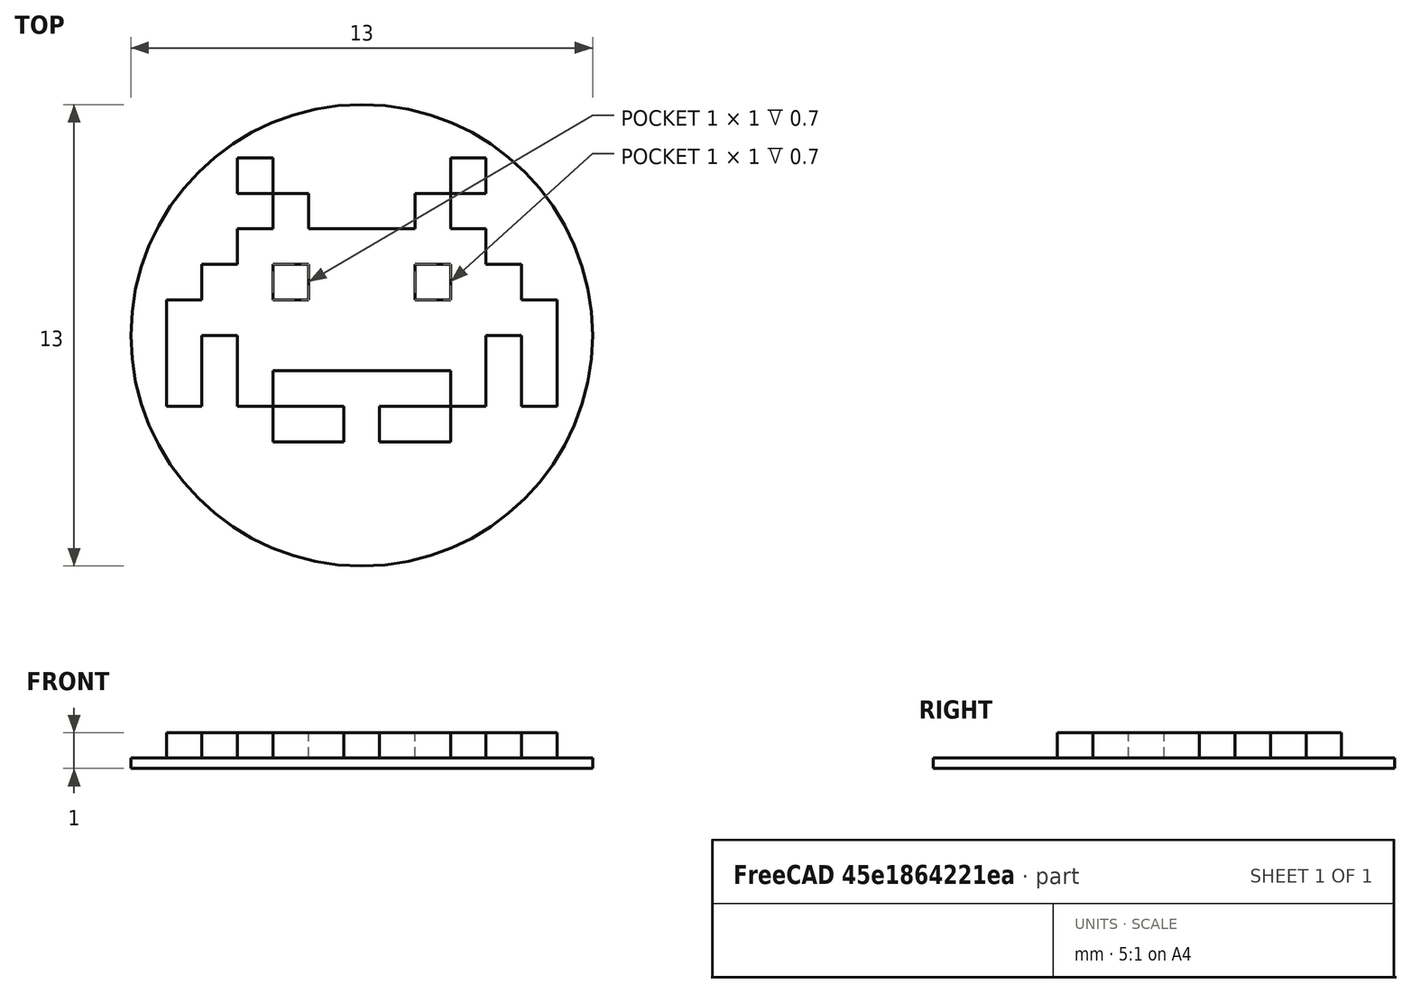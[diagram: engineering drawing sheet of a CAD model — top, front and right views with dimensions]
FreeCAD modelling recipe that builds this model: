
FCSTD DOCUMENT  (FreeCAD 0.20R29177 +233 (Git))
Label: pieza-marcianito
License: Creative Commons Attribution-ShareAlike
LicenseURL: http://creativecommons.org/licenses/by-sa/4.0/
objects: Part::Box×15, Part::MultiFuse×2, Part::Cylinder×1
note: 18 computed .brp shape members not serialized (recipe doc carries the construction recipe); baked Part::Feature solids carry a one-line shape summary decoded from their .brp

FEATURE [Part::Box] Box  label="Cubo"
  AttacherType = Attacher::AttachEngine3D
  Height = 1
  Length = 1
  Width = 1
FEATURE [Part::Box] Box001  label="Cubo001"
  AttacherType = Attacher::AttachEngine3D
  Height = 1
  Length = 1
  Placement = pos=(1,-2,0) rot=(0,0,1;0rad)
  Width = 2
FEATURE [Part::Box] Box002  label="Cubo002"
  AttacherType = Attacher::AttachEngine3D
  Height = 1
  Length = 3
  Placement = pos=(2,-5,0) rot=(0,0,1;0rad)
  Width = 4
FEATURE [Part::Box] Box003  label="Cubo003"
  AttacherType = Attacher::AttachEngine3D
  Height = 1
  Length = 1
  Placement = pos=(5,-2,0) rot=(0,0,1;0rad)
  Width = 2
FEATURE [Part::Box] Box004  label="Cubo004"
  AttacherType = Attacher::AttachEngine3D
  Height = 1
  Length = 1
  Placement = pos=(6,0,0) rot=(0,0,1;0rad)
  Width = 1
FEATURE [Part::Box] Box005  label="Cubo005"
  AttacherType = Attacher::AttachEngine3D
  Height = 1
  Length = 1
  Placement = pos=(0,-6,0) rot=(0,0,1;0rad)
  Width = 5
FEATURE [Part::Box] Box006  label="Cubo006"
  AttacherType = Attacher::AttachEngine3D
  Height = 1
  Length = 1
  Placement = pos=(6,-6,0) rot=(0,0,1;0rad)
  Width = 5
FEATURE [Part::Box] Box007  label="Cubo007"
  AttacherType = Attacher::AttachEngine3D
  Height = 1
  Length = 1
  Placement = pos=(1,-5,0) rot=(0,0,1;0rad)
  Width = 2
FEATURE [Part::Box] Box008  label="Cubo008"
  AttacherType = Attacher::AttachEngine3D
  Height = 1
  Length = 1
  Placement = pos=(5,-5,0) rot=(0,0,1;0rad)
  Width = 2
FEATURE [Part::Box] Box009  label="Cubo009"
  AttacherType = Attacher::AttachEngine3D
  Height = 1
  Length = 1
  Placement = pos=(-1,-4,0) rot=(0,0,1;0rad)
  Width = 2
FEATURE [Part::Box] Box010  label="Cubo010"
  AttacherType = Attacher::AttachEngine3D
  Height = 1
  Length = 1
  Placement = pos=(7,-4,0) rot=(0,0,1;0rad)
  Width = 2
FEATURE [Part::Box] Box011  label="Cubo011"
  AttacherType = Attacher::AttachEngine3D
  Height = 1
  Length = 1
  Placement = pos=(-2,-6,0) rot=(0,0,1;0rad)
  Width = 3
FEATURE [Part::Box] Box012  label="Cubo012"
  AttacherType = Attacher::AttachEngine3D
  Height = 1
  Length = 1
  Placement = pos=(8,-6,0) rot=(0,0,1;0rad)
  Width = 3
FEATURE [Part::Box] Box013  label="Cubo013"
  AttacherType = Attacher::AttachEngine3D
  Height = 1
  Length = 1
  Placement = pos=(3,-7,0) rot=(0,0,1;1.5708rad)
  Width = 2
FEATURE [Part::Box] Box014  label="Cubo014"
  AttacherType = Attacher::AttachEngine3D
  Height = 1
  Length = 1
  Placement = pos=(6,-7,0) rot=(0,0,1;1.5708rad)
  Width = 2
FEATURE [Part::MultiFuse] Fusion
  Refine = true
  Shapes = -> [Box,Box001,Box002,Box003,Box004,Box005,Box006,Box007,Box008,Box009,Box010,Box011,Box012,Box013,Box014]
FEATURE [Part::Cylinder] Cylinder  label="Cilindro"
  Angle = 360
  AttacherType = Attacher::AttachEngine3D
  FirstAngle = 0
  Height = 0.3
  Placement = pos=(3.5,-4,0) rot=(0,0,1;0rad)
  Radius = 6.5
  SecondAngle = 0
FEATURE [Part::MultiFuse] Fusion001
  Refine = true
  Shapes = -> [Fusion,Cylinder]
